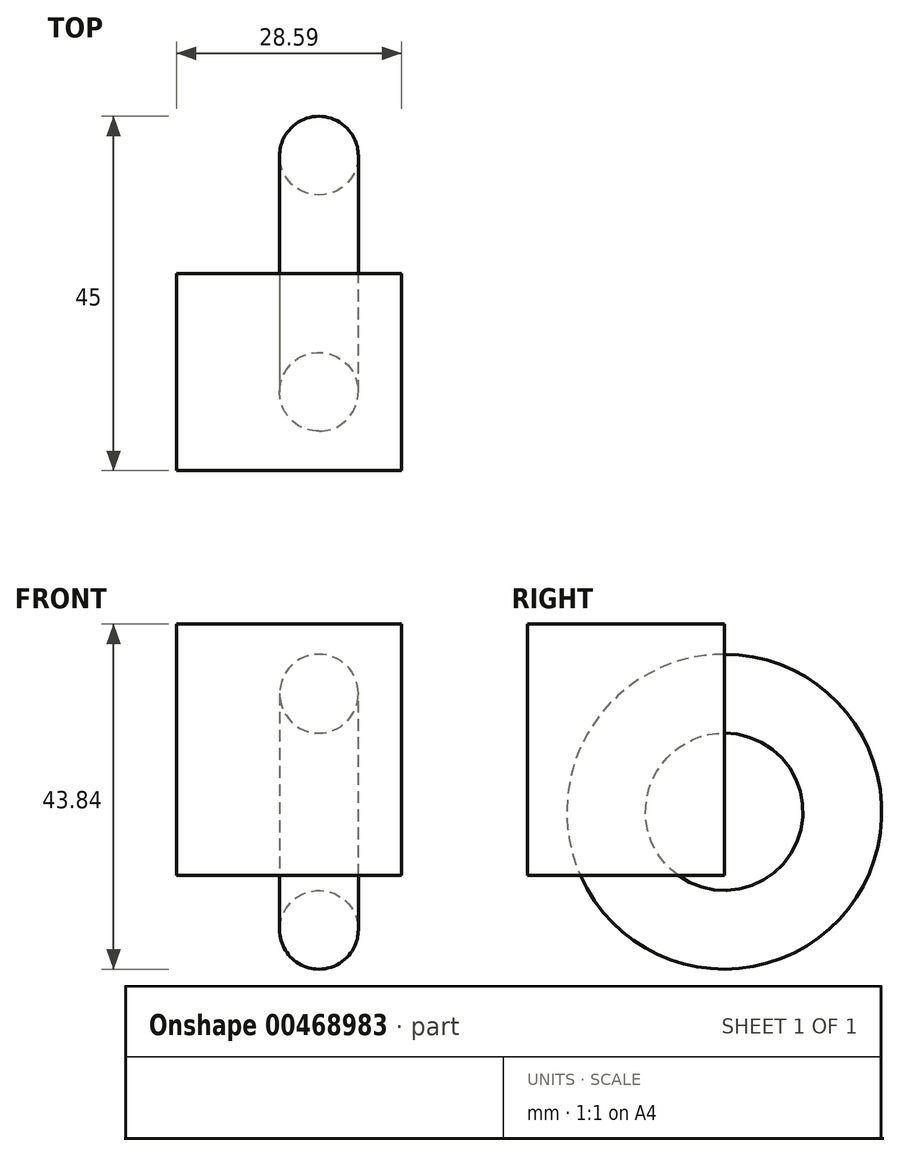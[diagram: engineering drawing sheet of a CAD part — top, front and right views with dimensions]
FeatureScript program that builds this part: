
annotation { "Feature Type Name" : "Feature", "Feature Type Description" : "" }
export const myFeature = defineFeature(function(context is Context, id is Id, definition is map)
    precondition{}
    {
        {
            var Q0;
            Q0=qCreatedBy(makeId("Front.planeOp"),FACE);
            var sketch = newSketch(context, id + "F0", { "sketchPlane" : qUnion([Q0])});
            skLineSegment(sketch, "E0", {"start": v(0, 0) * mm, "end": v(7.1, 0) * mm, "construction": true});
            skCircle(sketch, "E1", {"center": v(0, 15) * mm, "radius": 5 * mm});
            skPoint(sketch, "E2", {"position": v(0, 10) * mm});
            skSolve(sketch);
        }
        {
            var Q0;
            Q0=makeQuery(id+"F0.imprint","IMPRINT",FACE,{"disambiguationData":[TD([[makeQuery(id+"F0.imprint","IMPRINT",EDGE,{"derivedFrom":sQuery(id+"F0.wireOp",EDGE,"E1")}),1.0]])]});
            var Q1;
            Q1=sQuery(id+"F0.wireOp",EDGE,"E0");
            revolve(context, id + "F1", {"entities" : qUnion([Q0]), "axis" : qUnion([Q1]), "revolveType" : RevolveType.FULL});
        }
        {
            var Q0;
            Q0=qCreatedBy(makeId("Front.planeOp"),FACE);
            var sketch = newSketch(context, id + "F2", { "sketchPlane" : qUnion([Q0])});
            skLineSegment(sketch, "E3.bottom", {"start": v(-18.1, 23.84) * mm, "end": v(10.49, 23.84) * mm});
            skLineSegment(sketch, "E3.top", {"start": v(-18.1, -8.1) * mm, "end": v(10.49, -8.1) * mm});
            skLineSegment(sketch, "E3.left", {"start": v(-18.1, 23.84) * mm, "end": v(-18.1, -8.1) * mm});
            skLineSegment(sketch, "E3.right", {"start": v(10.49, 23.84) * mm, "end": v(10.49, -8.1) * mm});
            skSolve(sketch);
        }
        {
            var Q0;
            Q0 = qSketchRegion(id + "F2", true);
            extrude(context, id + "F3", {"entities" : qUnion([Q0]), "depth" : 25 * mm});
        }
    });
